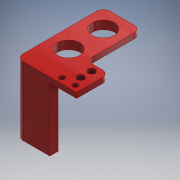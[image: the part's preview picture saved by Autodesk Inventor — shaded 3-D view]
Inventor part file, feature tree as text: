
AUTODESK INVENTOR PART (.ipt)
format: ipt  version: 2018.3 (Build 223284000, 284)  size: 374,272 bytes
history: native  units: mm
features: extrude x13, sketch x13, fillet x9, chamfer x2
ambient origin geometry x8: Origin, YZ Plane, XZ Plane, XY Plane, X Axis, Y Axis, Z Axis, Center Point
bodies: Solid1 (feature_tree)
feature tree (37):
  extrude  "Extrusion1"  Depth=4.0mm
  sketch  "Sketch2"  dims[d4=16.5mm d5=16.5mm]
  fillet  "Fillet3"  Radius=4.0mm
  extrude  "Extrusion5"  Depth=16.5mm
  extrude  "Extrusion8"  Depth=14.0mm
  fillet  "Fillet4"  Radius=25.883mm
  extrude  "Extrusion9"  Depth=4.0mm
  extrude  "Extrusion10"  Depth=4.0mm
  fillet  "Fillet6"  Radius=10.0mm
  extrude  "Extrusion11"  Depth=4.0mm
  extrude  "Extrusion12"  Depth=22.0mm
  extrude  "Extrusion14"  Depth=1.0mm
  extrude  "Extrusion15"  Depth=3.0mm
  extrude  "Extrusion16"  Depth=3.0mm TaperAngle=0.0deg
  chamfer  "Chamfer1"  Distance=5.0mm
  extrude  "Extrusion17"  Depth=2.0mm
  fillet  "Fillet9"  Radius=8.1mm
  extrude  "Extrusion18"  Depth=10.0mm TaperAngle=0.0deg
  extrude  "Extrusion19"  Depth=2.0mm
  fillet  "Fillet10"  Radius=3.0mm
  fillet  "Fillet11"  Radius=48.0mm
  fillet  "Fillet12"  Radius=1.5mm
  fillet  "Fillet13"  Radius=30.0mm
  fillet  "Fillet14"  Radius=3.925mm
  chamfer  "Chamfer2"  Distance=12.2915mm
  sketch  "Sketch1"  dims[d0=45.0mm d1=65.0mm d2=4.0mm d3=0.0mm]
  sketch  "Sketch4"  dims[d6=14.0mm d7=14.0mm d8=25.883mm]
  sketch  "Sketch6"  dims[d19=5.0mm d20=4.0mm]
  sketch  "Sketch7"  dims[d21=5.0mm d22=4.0mm d24=10.0mm]
  sketch  "Sketch8"  dims[d25=0.0mm d26=0.0mm d27=4.0mm]
  sketch  "Sketch9"  dims[d34=22.0mm d35=22.0mm]
  sketch  "Sketch10"  dims[d36=3.0mm d37=0.0mm d38=1.0mm]
  sketch  "Sketch11"  dims[d39=3.0mm d40=0.0mm d41=20.2mm]
  sketch  "Sketch12"  dims[d42=14.0mm d43=3.0mm d44=0.0mm]
  sketch  "Sketch13"  dims[d46=5.0mm]
  sketch  "Sketch14"  dims[d47=5.4mm]
  sketch  "Sketch15"  dims[d48=8.1mm d49=5.0mm d50=5.4mm d51=8.1mm d52=10.0mm d53=0.0mm d54=20.0mm d55=3.0mm d56=48.0mm d57=0.0mm d62=1.5mm d63=30.0mm d65=3.925mm d66=12.2915mm d67=10.0mm d68=90.0deg d71=10.0mm d72=15.0mm d73=3.0mm d74=1.0mm d75=1.0mm d76=0.0mm d77=7.5mm d78=4.0mm d79=0.0mm d80=3.0mm d81=2.5mm d82=2.5mm d83=4.0mm d84=0.0mm d85=2.5mm d86=4.0mm d87=45.0deg d88=5.0mm d89=1.5mm d90=4.0mm d91=5.0mm d92=1.5mm d93=3.0mm d94=3.0mm d95=0.0mm d98=1.5mm d99=2.0mm d100=0.0mm d101=2.0mm d102=2.0mm d103=90.0deg d104=2.0mm d105=0.0mm d106=0.5mm d107=0.5mm d108=1.0mm d109=1.0mm d110=1.0mm d111=1.0mm d112=2.0mm d113=45.0deg]
